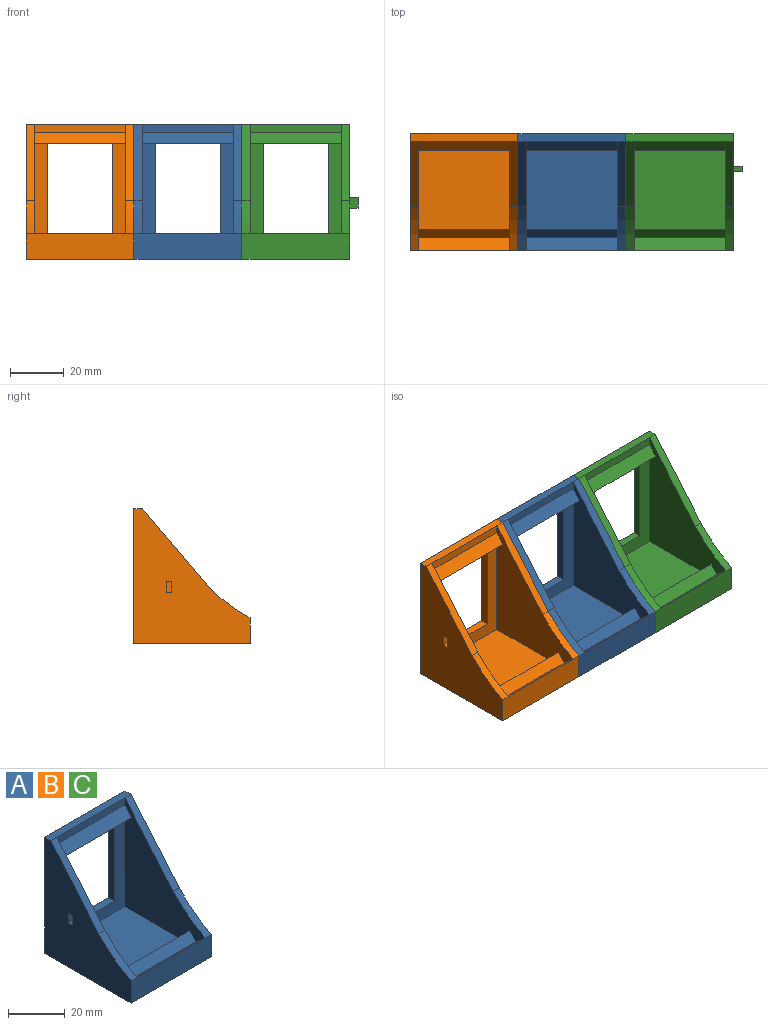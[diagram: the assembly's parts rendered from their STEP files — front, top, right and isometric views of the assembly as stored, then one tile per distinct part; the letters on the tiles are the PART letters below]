
ASSEMBLY  parts=3 mates=8
PART A: 32 faces, bbox 43x43x50 mm
  f0: plane 28.23x24.03mm, normal (0,-0.76,0.65), area 111.2mm2, adj f3,f10,f14,f30
  f1: plane 34x4.73mm, normal (0,0.65,0.76), area 211.2mm2, adj f2,f3,f16,f19
  f2: plane 47x40mm, normal (-1,0,0), area 940.3mm2, adj f1,f4,f5,f8,f9,f17,f18,f19
  f3: plane 47x40mm, normal (1,0,0), area 932.3mm2, adj f0,f1,f5,f8,f9,f17,f18,f19
  f4: plane 28.23x24.03mm, normal (0,-0.76,0.65), area 111.2mm2, adj f2,f12,f14,f31
  f5: plane 40.11x34mm, normal (0,-1,0), area 521.1mm2, adj f2,f3,f6,f7,f8,f13,f18
  f6: plane 35.11x3mm, normal (1,0,0), area 105.3mm2, adj f5,f13,f15,f18
  f7: plane 35.11x3mm, normal (-1,0,0), area 105.3mm2, adj f5,f13,f15,f18
  f8: plane 34x32.36mm, normal (0,0,1), area 1100.3mm2, adj f2,f3,f5,f20
  f9: plane 34x3.09mm, normal (0,-1,0), area 104.9mm2, adj f2,f3,f14,f17
  f10: plane 50x43mm, normal (-1,0,0), area 1241.9mm2, adj f0,f11,f14,f15,f16,f26,f27,f28
  f11: plane 43x40mm, normal (0,0,-1), area 1720mm2, adj f10,f12,f15,f16
  f12: plane 50x43mm, normal (1,0,0), area 1241.9mm2, adj f4,f11,f14,f15,f16,f21,f22,f23
  f13: plane 24x3mm, normal (0,0,1), area 72mm2, adj f5,f6,f7,f15
  f14: plane 40x3mm, normal (0,0,1), area 120mm2, adj f0,f4,f9,f10,f12,f15
  f15: plane 50x40mm, normal (0,1,0), area 1157.4mm2, adj f6,f7,f10,f11,f12,f13,f14,f18
  f16: plane 40x9.5mm, normal (0,-1,0), area 380mm2, adj f1,f10,f11,f12,f30,f31
  f17: plane 34x3.81mm, normal (0,-0.76,0.65), area 170mm2, adj f2,f3,f9,f18
  f18: plane 34x6.24mm, normal (0,0,-1), area 182.2mm2, adj f2,f3,f5,f6,f7,f15,f17
  f19: plane 34x3.42mm, normal (0,-0.76,0.65), area 152.5mm2, adj f1,f2,f3,f20
  f20: plane 34x5.89mm, normal (0,1,0), area 200.2mm2, adj f2,f3,f8,f19
  f21: plane 4x3mm, normal (0,-1,0), area 12mm2, adj f12,f22,f24,f25
  f22: plane 3x2mm, normal (0,0,-1), area 6mm2, adj f12,f21,f23,f25
  f23: plane 4x3mm, normal (0,1,0), area 12mm2, adj f12,f22,f24,f25
  f24: plane 3x2mm, normal (0,0,1), area 6mm2, adj f12,f21,f23,f25
  f25: plane 4x2mm, normal (1,0,0), area 8mm2, adj f21,f22,f23,f24
  f26: plane 4x3mm, normal (0,-1,0), area 12mm2, adj f3,f10,f27,f29
  f27: plane 3x2mm, normal (0,0,1), area 6mm2, adj f3,f10,f26,f28
  f28: plane 4x3mm, normal (0,1,0), area 12mm2, adj f3,f10,f27,f29
  f29: plane 3x2mm, normal (0,0,-1), area 6mm2, adj f3,f10,f26,f28
  f30: cylinder r=57mm len=15.97mm, axis (-1,0,0), area 60.7mm2, adj f0,f3,f10,f16
  f31: cylinder r=57mm len=15.97mm, axis (1,0,0), area 60.7mm2, adj f2,f4,f12,f16
PART B: same geometry as A
PART C: same geometry as A
PLACE A t=(-30.13,30.84,-22.42)mm
PLACE B t=(-70.13,30.84,-22.42)mm fixed
PLACE C t=(9.87,30.84,-22.42)mm
MATE planar A.f3 <-> B.f25  axis (1,0,0) through (-87.13,18.84,18.58)mm
MATE planar A.f25 <-> C.f3  axis (1,0,0) through (-47.13,17.84,18.58)mm
MATE planar A.f11 <-> C.f11  axis (0,0,-1) through (-70.13,9.34,-2.42)mm
MATE planar C.f16 <-> A.f16  axis (0,-1,0) through (-30.13,-12.16,2.33)mm
MATE planar A.f16 <-> B.f16  axis (0,-1,0) through (-70.13,-12.16,-2.42)mm
MATE parallel B.f12 <-> C.f10  axis (1,0,0) through (-90.13,9.34,-2.42)mm
MATE parallel A.f12 <-> C.f10  axis (1,0,0) through (-50.13,9.34,-2.42)mm
MATE planar A.f11 <-> B.f11  axis (0,0,-1) through (-90.13,9.34,-2.42)mm
